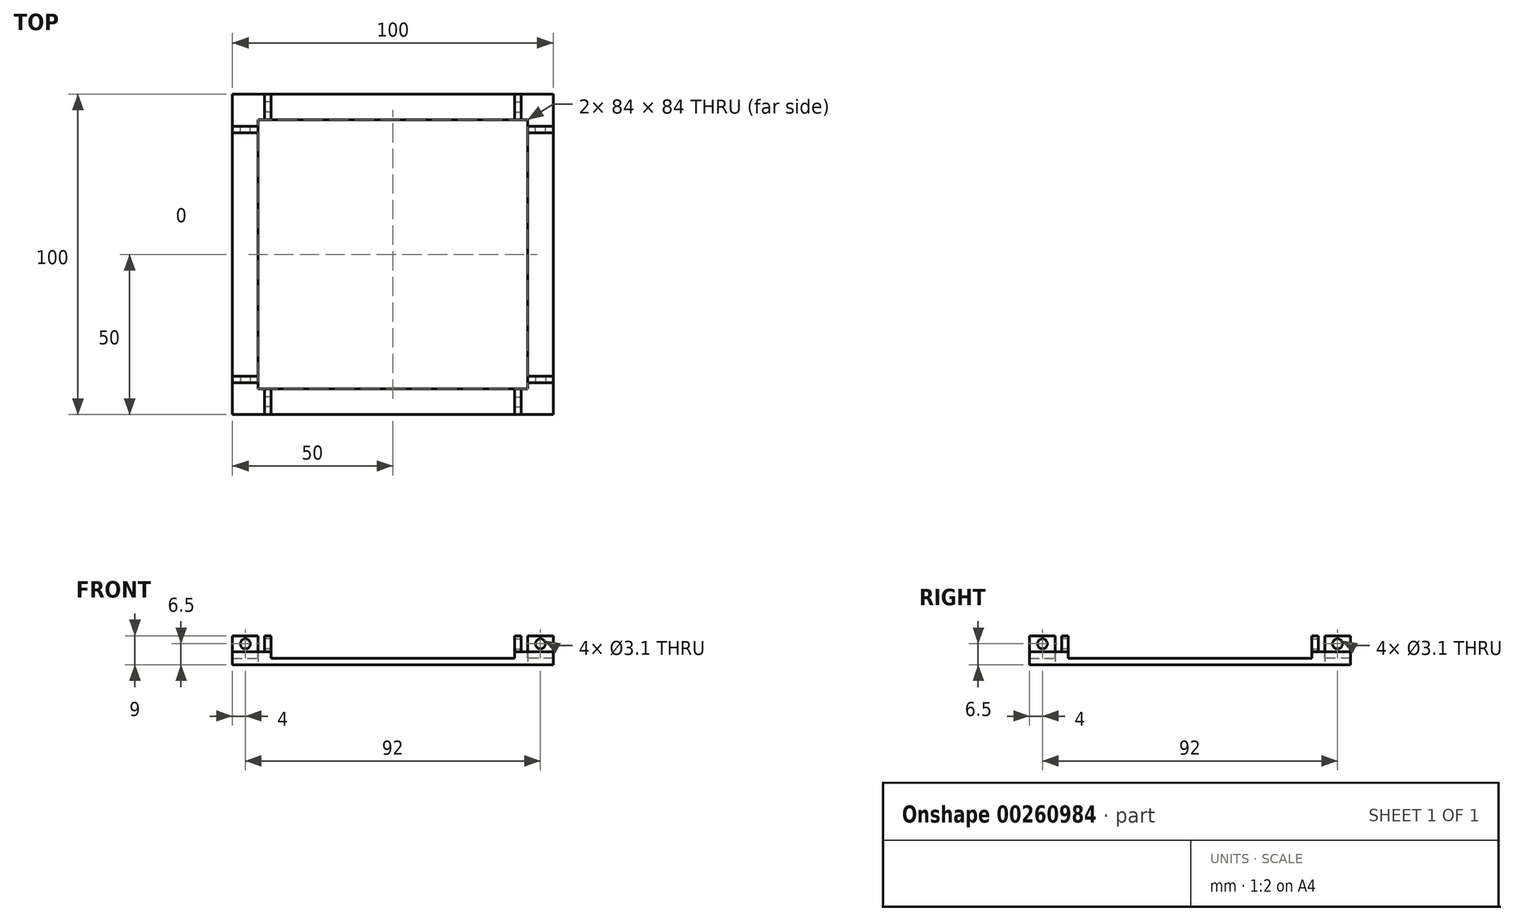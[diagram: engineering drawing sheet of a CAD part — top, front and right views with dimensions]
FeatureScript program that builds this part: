
annotation { "Feature Type Name" : "Feature", "Feature Type Description" : "" }
export const myFeature = defineFeature(function(context is Context, id is Id, definition is map)
    precondition{}
    {
        {
            var Q0;
            Q0=qCreatedBy(makeId("Top.planeOp"),FACE);
            var sketch = newSketch(context, id + "F0", { "sketchPlane" : qUnion([Q0])});
            skLineSegment(sketch, "E0", {"start": v(0, 0) * mm, "end": v(100, 0) * mm});
            skLineSegment(sketch, "E1", {"start": v(100, 0) * mm, "end": v(100, 100) * mm});
            skLineSegment(sketch, "E2", {"start": v(100, 100) * mm, "end": v(0, 100) * mm});
            skLineSegment(sketch, "E3", {"start": v(0, 100) * mm, "end": v(0, 0) * mm});
            skLineSegment(sketch, "E4", {"start": v(0, 0) * mm, "end": v(8, 0) * mm});
            skLineSegment(sketch, "E5", {"start": v(8, 8) * mm, "end": v(8, 92) * mm});
            skLineSegment(sketch, "E6", {"start": v(8, 92) * mm, "end": v(92, 92) * mm});
            skLineSegment(sketch, "E7", {"start": v(92, 92) * mm, "end": v(92, 8) * mm});
            skLineSegment(sketch, "E8", {"start": v(92, 8) * mm, "end": v(8, 8) * mm});
            skLineSegment(sketch, "E9", {"start": v(50, 0) * mm, "end": v(50, 8) * mm, "construction": true});
            skSolve(sketch);
        }
        {
            var Q0;
            Q0=makeQuery(id+"F0.imprint","IMPRINT",FACE,{"disambiguationData":[TD([[makeQuery(id+"F0.imprint","IMPRINT",EDGE,{"derivedFrom":sQuery(id+"F0.wireOp",EDGE,"E0")}),1.0]])]});
            extrude(context, id + "F1", {"entities" : qUnion([Q0]), "depth" : 8 * mm});
        }
        {
            var Q0;
            Q0=makeQuery(id+"F1.opExtrude","CAP_FACE",FACE,{"disambiguationData":[OSD([sQuery(id+"F0.wireOp",EDGE,"E0"),sQuery(id+"F0.wireOp",EDGE,"E1"),sQuery(id+"F0.wireOp",EDGE,"E2"),sQuery(id+"F0.wireOp",EDGE,"E3"),sQuery(id+"F0.wireOp",EDGE,"E4"),sQuery(id+"F0.wireOp",EDGE,"E5"),sQuery(id+"F0.wireOp",EDGE,"E6"),sQuery(id+"F0.wireOp",EDGE,"E7"),sQuery(id+"F0.wireOp",EDGE,"E8")])],"isStart":false});
            var sketch = newSketch(context, id + "F2", { "sketchPlane" : qUnion([Q0])});
            skLineSegment(sketch, "E10.0", {"start": v(92, 8) * mm, "end": v(8, 8) * mm, "construction": true});
            skLineSegment(sketch, "E11.0", {"start": v(0, 0) * mm, "end": v(100, 0) * mm, "construction": true});
            skLineSegment(sketch, "E12", {"start": v(8, 8) * mm, "end": v(8, 0) * mm});
            skLineSegment(sketch, "E13", {"start": v(8, 0) * mm, "end": v(12, 0) * mm});
            skLineSegment(sketch, "E14", {"start": v(12, 0) * mm, "end": v(12, 8) * mm});
            skLineSegment(sketch, "E15", {"start": v(12, 8) * mm, "end": v(8, 8) * mm});
            skSolve(sketch);
        }
        {
            var Q0;
            Q0=makeQuery(id+"F2.imprint","IMPRINT",FACE,{"disambiguationData":[TD([[makeQuery(id+"F2.imprint","IMPRINT",EDGE,{"derivedFrom":sQuery(id+"F2.wireOp",EDGE,"E12")}),1.0]])]});
            extrude(context, id + "F3", {"entities" : qUnion([Q0]), "operationType" : NewBodyOperationType.ADD, "depth" : 5 * mm});
        }
        {
            var Q0;
            Q0=makeQuery(id+"F3.opExtrude","SWEPT_FACE",FACE,{"disambiguationData":[OSD([sQuery(id+"F2.wireOp",EDGE,"E12")])]});
            var sketch = newSketch(context, id + "F4", { "sketchPlane" : qUnion([Q0])});
            skLineSegment(sketch, "E16.0", {"start": v(-8, 13) * mm, "end": v(0, 13) * mm, "construction": true});
            skLineSegment(sketch, "E17.0", {"start": v(-8, 13) * mm, "end": v(-8, 8) * mm, "construction": true});
            skLineSegment(sketch, "E18.0", {"start": v(-100, 8) * mm, "end": v(0, 8) * mm, "construction": true});
            skLineSegment(sketch, "E19.0", {"start": v(0, 13) * mm, "end": v(0, 8) * mm, "construction": true});
            skLineSegment(sketch, "E20", {"start": v(-4, 13) * mm, "end": v(-4, 8) * mm, "construction": true});
            skCircle(sketch, "E21", {"center": v(-4, 10.5) * mm, "radius": 1.55 * mm});
            skSolve(sketch);
        }
        {
            var Q0;
            Q0=makeQuery(id+"F4.imprint","IMPRINT",FACE,{"disambiguationData":[TD([[makeQuery(id+"F4.imprint","IMPRINT",EDGE,{"derivedFrom":sQuery(id+"F4.wireOp",EDGE,"53860cc5-d47c-4bca-ac85-03c5c8d22e110.MirrorCS")}),-1.0]])]});
            var Q1;
            Q1=makeQuery(id+"F4.imprint","IMPRINT",FACE,{"disambiguationData":[TD([[makeQuery(id+"F4.imprint","IMPRINT",EDGE,{"derivedFrom":sQuery(id+"F4.wireOp",EDGE,"E21")}),1.0]])]});
            var Q2;
            Q2=makeQuery(id+"F4.imprint","IMPRINT",FACE,{"disambiguationData":[TD([[makeQuery(id+"F4.imprint","IMPRINT",EDGE,{"derivedFrom":sQuery(id+"F4.wireOp",EDGE,"ADuCnaiS-x6I3-Dmo5-K39o-WolqJzbKUGD2")}),1.0]])]});
            extrude(context, id + "F5", {"entities" : qUnion([Q0, Q1, Q2]), "operationType" : NewBodyOperationType.REMOVE, "oppositeDirection" : true, "depth" : 5 * mm});
        }
        {
            var Q0;
            Q0=makeQuery(id+"F1.opExtrude","CAP_FACE",FACE,{"disambiguationData":[OSD([sQuery(id+"F0.wireOp",EDGE,"E0"),sQuery(id+"F0.wireOp",EDGE,"E1"),sQuery(id+"F0.wireOp",EDGE,"E2"),sQuery(id+"F0.wireOp",EDGE,"E3"),sQuery(id+"F0.wireOp",EDGE,"E4"),sQuery(id+"F0.wireOp",EDGE,"E5"),sQuery(id+"F0.wireOp",EDGE,"E6"),sQuery(id+"F0.wireOp",EDGE,"E7"),sQuery(id+"F0.wireOp",EDGE,"E8")])],"isStart":false});
            var sketch = newSketch(context, id + "F6", { "sketchPlane" : qUnion([Q0])});
            skLineSegment(sketch, "E22.0", {"start": v(12, 0) * mm, "end": v(100, 0) * mm});
            skLineSegment(sketch, "E23.0", {"start": v(12, 8) * mm, "end": v(8, 8) * mm, "construction": true});
            skLineSegment(sketch, "E24.0", {"start": v(0, 0) * mm, "end": v(8, 0) * mm, "construction": true});
            skLineSegment(sketch, "E25", {"start": v(12, 0) * mm, "end": v(50, 0) * mm});
            skLineSegment(sketch, "E26", {"start": v(50, 0) * mm, "end": v(50, 8) * mm});
            skLineSegment(sketch, "E27", {"start": v(50, 8) * mm, "end": v(52, 8) * mm});
            skLineSegment(sketch, "E28", {"start": v(52, 8) * mm, "end": v(52, 0) * mm});
            skSolve(sketch);
        }
        {
            var Q0;
            {var subQ0=sQuery(id+"F6.wireOp",EDGE,"E26");Q0=makeQuery(id+"F6.imprint","IMPRINT",FACE,{"disambiguationData":[TD([[makeQuery(id+"F6.imprint","IMPRINT",EDGE,{"derivedFrom":subQ0}),-1.0]])]});}
            extrude(context, id + "F7", {"entities" : qUnion([Q0]), "operationType" : NewBodyOperationType.ADD, "depth" : 25 * mm});
        }
        {
            var Q0;
            Q0=makeQuery(id+"F1.opExtrude","SWEPT_BODY",BODY,{"disambiguationData":[OSD([sQuery(id+"F0.wireOp",EDGE,"E0"),sQuery(id+"F0.wireOp",EDGE,"E1"),sQuery(id+"F0.wireOp",EDGE,"E2"),sQuery(id+"F0.wireOp",EDGE,"E3"),sQuery(id+"F0.wireOp",EDGE,"E4"),sQuery(id+"F0.wireOp",EDGE,"E5"),sQuery(id+"F0.wireOp",EDGE,"E6"),sQuery(id+"F0.wireOp",EDGE,"E7"),sQuery(id+"F0.wireOp",EDGE,"E8")])]});
            var Q1;
            Q1=makeQuery(id+"F7.opExtrude","SWEPT_FACE",FACE,{"disambiguationData":[OSD([sQuery(id+"F6.wireOp",EDGE,"E26")])]});
            mirror(context, id + "F8", {"operationType" : NewBodyOperationType.ADD, "entities" : qUnion([Q0]), "mirrorPlane" : qUnion([Q1])});
        }
        {
            var Q0;
            {var subQ0=makeQuery(id+"F7.boolean.opBoolean","MERGE",FACE,{"derivedFrom":[makeQuery(id+"F3.boolean.opBoolean","MERGE",FACE,{"derivedFrom":[makeQuery(id+"F1.opExtrude","SWEPT_FACE",FACE,{"disambiguationData":[OSD([sQuery(id+"F0.wireOp",EDGE,"E8")])]}),makeQuery(id+"F3.opExtrude","SWEPT_FACE",FACE,{"disambiguationData":[OSD([sQuery(id+"F2.wireOp",EDGE,"E15")])]})]}),makeQuery(id+"F7.opExtrude","SWEPT_FACE",FACE,{"disambiguationData":[OSD([sQuery(id+"F6.wireOp",EDGE,"E27")])]})]});Q0=makeQuery(id+"F8.boolean.opBoolean","MERGE",FACE,{"derivedFrom":[subQ0,makeQuery(id+"F8.opPattern","COPY",FACE,{"derivedFrom":subQ0,"instanceName":"1"})]});}
            var sketch = newSketch(context, id + "F9", { "sketchPlane" : qUnion([Q0])});
            skLineSegment(sketch, "E29", {"start": v(-48, 8) * mm, "end": v(-50, 8) * mm});
            skLineSegment(sketch, "E30", {"start": v(-50, 8) * mm, "end": v(-50, 33) * mm});
            skLineSegment(sketch, "E31", {"start": v(-50, 33) * mm, "end": v(-48, 33) * mm});
            skLineSegment(sketch, "E32", {"start": v(-48, 33) * mm, "end": v(-48, 8) * mm});
            skSolve(sketch);
        }
        {
            var Q0;
            Q0=makeQuery(id+"F9.imprint","IMPRINT",FACE,{"disambiguationData":[TD([[makeQuery(id+"F9.imprint","IMPRINT",EDGE,{"derivedFrom":sQuery(id+"F9.wireOp",EDGE,"E29")}),-1.0]])]});
            extrude(context, id + "F10", {"entities" : qUnion([Q0]), "operationType" : NewBodyOperationType.ADD, "depth" : 42 * mm});
        }
        {
            var Q0;
            Q0=makeQuery(id+"F1.opExtrude","SWEPT_BODY",BODY,{"disambiguationData":[OSD([sQuery(id+"F0.wireOp",EDGE,"E0"),sQuery(id+"F0.wireOp",EDGE,"E1"),sQuery(id+"F0.wireOp",EDGE,"E2"),sQuery(id+"F0.wireOp",EDGE,"E3"),sQuery(id+"F0.wireOp",EDGE,"E4"),sQuery(id+"F0.wireOp",EDGE,"E5"),sQuery(id+"F0.wireOp",EDGE,"E6"),sQuery(id+"F0.wireOp",EDGE,"E7"),sQuery(id+"F0.wireOp",EDGE,"E8")])]});
            var Q1;
            Q1=makeQuery(id+"F10.opExtrude","CAP_EDGE",EDGE,{"disambiguationData":[OSD([sQuery(id+"F9.wireOp",EDGE,"E30")])],"isStart":false});
            circularPattern(context, id + "F11", {"entities" : qUnion([Q0]), "axis" : qUnion([Q1]), "angle" : 360 * degree, "instanceCount" : 4, "equalSpace" : true});
        }
        {
            var Q0;
            {var subQ0=makeQuery(id+"F7.opExtrude","CAP_FACE",FACE,{"disambiguationData":[OSD([sQuery(id+"F6.wireOp",EDGE,"E22.0"),sQuery(id+"F6.wireOp",EDGE,"E26"),sQuery(id+"F6.wireOp",EDGE,"E27"),sQuery(id+"F6.wireOp",EDGE,"E28")])],"isStart":false});Q0=makeQuery(id+"F11.opPattern","COPY",FACE,{"derivedFrom":makeQuery(id+"F10.boolean.opBoolean","MERGE",FACE,{"derivedFrom":[makeQuery(id+"F8.boolean.opBoolean","MERGE",FACE,{"derivedFrom":[subQ0,makeQuery(id+"F8.opPattern","COPY",FACE,{"derivedFrom":subQ0,"instanceName":"1"})]}),makeQuery(id+"F10.opExtrude","SWEPT_FACE",FACE,{"disambiguationData":[OSD([sQuery(id+"F9.wireOp",EDGE,"E31")])]})]}),"instanceName":"1"});}
            var Q1;
            {var subQ0=makeQuery(id+"F7.opExtrude","CAP_FACE",FACE,{"disambiguationData":[OSD([sQuery(id+"F6.wireOp",EDGE,"E22.0"),sQuery(id+"F6.wireOp",EDGE,"E26"),sQuery(id+"F6.wireOp",EDGE,"E27"),sQuery(id+"F6.wireOp",EDGE,"E28")])],"isStart":false});Q1=makeQuery(id+"F11.opPattern","COPY",FACE,{"derivedFrom":makeQuery(id+"F10.boolean.opBoolean","MERGE",FACE,{"derivedFrom":[makeQuery(id+"F8.boolean.opBoolean","MERGE",FACE,{"derivedFrom":[subQ0,makeQuery(id+"F8.opPattern","COPY",FACE,{"derivedFrom":subQ0,"instanceName":"1"})]}),makeQuery(id+"F10.opExtrude","SWEPT_FACE",FACE,{"disambiguationData":[OSD([sQuery(id+"F9.wireOp",EDGE,"E31")])]})]}),"instanceName":"2"});}
            var Q2;
            {var subQ0=makeQuery(id+"F7.opExtrude","CAP_FACE",FACE,{"disambiguationData":[OSD([sQuery(id+"F6.wireOp",EDGE,"E22.0"),sQuery(id+"F6.wireOp",EDGE,"E26"),sQuery(id+"F6.wireOp",EDGE,"E27"),sQuery(id+"F6.wireOp",EDGE,"E28")])],"isStart":false});Q2=makeQuery(id+"F11.opPattern","COPY",FACE,{"derivedFrom":makeQuery(id+"F10.boolean.opBoolean","MERGE",FACE,{"derivedFrom":[makeQuery(id+"F8.boolean.opBoolean","MERGE",FACE,{"derivedFrom":[subQ0,makeQuery(id+"F8.opPattern","COPY",FACE,{"derivedFrom":subQ0,"instanceName":"1"})]}),makeQuery(id+"F10.opExtrude","SWEPT_FACE",FACE,{"disambiguationData":[OSD([sQuery(id+"F9.wireOp",EDGE,"E31")])]})]}),"instanceName":"3"});}
            var Q3;
            {var subQ0=makeQuery(id+"F7.opExtrude","CAP_FACE",FACE,{"disambiguationData":[OSD([sQuery(id+"F6.wireOp",EDGE,"E22.0"),sQuery(id+"F6.wireOp",EDGE,"E26"),sQuery(id+"F6.wireOp",EDGE,"E27"),sQuery(id+"F6.wireOp",EDGE,"E28")])],"isStart":false});Q3=makeQuery(id+"F10.boolean.opBoolean","MERGE",FACE,{"derivedFrom":[makeQuery(id+"F8.boolean.opBoolean","MERGE",FACE,{"derivedFrom":[subQ0,makeQuery(id+"F8.opPattern","COPY",FACE,{"derivedFrom":subQ0,"instanceName":"1"})]}),makeQuery(id+"F10.opExtrude","SWEPT_FACE",FACE,{"disambiguationData":[OSD([sQuery(id+"F9.wireOp",EDGE,"E31")])]})]});}
            extrude(context, id + "F12", {"entities" : qUnion([Q0, Q1, Q2, Q3]), "operationType" : NewBodyOperationType.REMOVE, "oppositeDirection" : true, "depth" : 25 * mm});
        }
        {
            var Q0;
            Q0=makeQuery(id+"F11.opPattern","COPY",FACE,{"derivedFrom":makeQuery(id+"F3.opExtrude","SWEPT_FACE",FACE,{"disambiguationData":[OSD([sQuery(id+"F2.wireOp",EDGE,"E12")])]}),"instanceName":"2"});
            var Q1;
            Q1=makeQuery(id+"F8.opPattern","COPY",FACE,{"derivedFrom":makeQuery(id+"F3.opExtrude","SWEPT_FACE",FACE,{"disambiguationData":[OSD([sQuery(id+"F2.wireOp",EDGE,"E12")])]}),"instanceName":"1"});
            extrude(context, id + "F13", {"entities" : qUnion([Q0, Q1]), "operationType" : NewBodyOperationType.REMOVE, "oppositeDirection" : true, "depth" : 2 * mm});
        }
        {
            var Q0;
            Q0=makeQuery(id+"F11.opPattern","COPY",FACE,{"derivedFrom":makeQuery(id+"F3.opExtrude","SWEPT_FACE",FACE,{"disambiguationData":[OSD([sQuery(id+"F2.wireOp",EDGE,"E12")])]}),"instanceName":"1"});
            var Q1;
            Q1=makeQuery(id+"F11.opPattern","COPY",FACE,{"derivedFrom":makeQuery(id+"F8.opPattern","COPY",FACE,{"derivedFrom":makeQuery(id+"F3.opExtrude","SWEPT_FACE",FACE,{"disambiguationData":[OSD([sQuery(id+"F2.wireOp",EDGE,"E12")])]}),"instanceName":"1"}),"instanceName":"3"});
            extrude(context, id + "F14", {"entities" : qUnion([Q0, Q1]), "operationType" : NewBodyOperationType.REMOVE, "oppositeDirection" : true, "depth" : 2 * mm});
        }
        {
            var Q0;
            Q0=makeQuery(id+"F3.opExtrude","SWEPT_FACE",FACE,{"disambiguationData":[OSD([sQuery(id+"F2.wireOp",EDGE,"E12")])]});
            var Q1;
            Q1=makeQuery(id+"F11.opPattern","COPY",FACE,{"derivedFrom":makeQuery(id+"F8.opPattern","COPY",FACE,{"derivedFrom":makeQuery(id+"F3.opExtrude","SWEPT_FACE",FACE,{"disambiguationData":[OSD([sQuery(id+"F2.wireOp",EDGE,"E12")])]}),"instanceName":"1"}),"instanceName":"2"});
            extrude(context, id + "F15", {"entities" : qUnion([Q0, Q1]), "operationType" : NewBodyOperationType.REMOVE, "oppositeDirection" : true, "depth" : 2 * mm});
        }
        {
            var Q0;
            Q0=makeQuery(id+"F11.opPattern","COPY",FACE,{"derivedFrom":makeQuery(id+"F8.opPattern","COPY",FACE,{"derivedFrom":makeQuery(id+"F3.opExtrude","SWEPT_FACE",FACE,{"disambiguationData":[OSD([sQuery(id+"F2.wireOp",EDGE,"E12")])]}),"instanceName":"1"}),"instanceName":"1"});
            var Q1;
            Q1=makeQuery(id+"F11.opPattern","COPY",FACE,{"derivedFrom":makeQuery(id+"F3.opExtrude","SWEPT_FACE",FACE,{"disambiguationData":[OSD([sQuery(id+"F2.wireOp",EDGE,"E12")])]}),"instanceName":"3"});
            extrude(context, id + "F16", {"entities" : qUnion([Q0, Q1]), "operationType" : NewBodyOperationType.REMOVE, "oppositeDirection" : true, "depth" : 2 * mm});
        }
        {
            var Q0;
            Q0=makeQuery(id+"F11.opPattern","COPY",FACE,{"derivedFrom":makeQuery(id+"F1.opExtrude","CAP_FACE",FACE,{"disambiguationData":[OSD([sQuery(id+"F0.wireOp",EDGE,"E0"),sQuery(id+"F0.wireOp",EDGE,"E1"),sQuery(id+"F0.wireOp",EDGE,"E2"),sQuery(id+"F0.wireOp",EDGE,"E3"),sQuery(id+"F0.wireOp",EDGE,"E4"),sQuery(id+"F0.wireOp",EDGE,"E5"),sQuery(id+"F0.wireOp",EDGE,"E6"),sQuery(id+"F0.wireOp",EDGE,"E7"),sQuery(id+"F0.wireOp",EDGE,"E8")])],"isStart":true}),"instanceName":"2"});
            extrude(context, id + "F17", {"entities" : qUnion([Q0]), "operationType" : NewBodyOperationType.REMOVE, "oppositeDirection" : true, "depth" : 4 * mm});
        }
        {
            var Q0;
            {var subQ0=sQuery(id+"F9.wireOp",EDGE,"E31");var subQ1=sQuery(id+"F6.wireOp",EDGE,"E28");var subQ2=sQuery(id+"F6.wireOp",EDGE,"E27");var subQ3=sQuery(id+"F6.wireOp",EDGE,"E26");var subQ4=sQuery(id+"F6.wireOp",EDGE,"E22.0");var subQ5=makeQuery(id+"F7.opExtrude","CAP_FACE",FACE,{"disambiguationData":[OSD([subQ4,subQ3,subQ2,subQ1])],"isStart":false});var subQ6=makeQuery(id+"F10.boolean.opBoolean","MERGE",FACE,{"derivedFrom":[makeQuery(id+"F8.boolean.opBoolean","MERGE",FACE,{"derivedFrom":[subQ5,makeQuery(id+"F8.opPattern","COPY",FACE,{"derivedFrom":subQ5,"instanceName":"1"})]}),makeQuery(id+"F10.opExtrude","SWEPT_FACE",FACE,{"disambiguationData":[OSD([subQ0])]})]});var subQ10=sQuery(id+"F0.wireOp",EDGE,"E8");var subQ12=sQuery(id+"F0.wireOp",EDGE,"E4");var subQ13=sQuery(id+"F0.wireOp",EDGE,"E0");var subQ16=makeQuery(id+"F7.opExtrude","SWEPT_FACE",FACE,{"disambiguationData":[OSD([subQ1])]});var subQ17=makeQuery(id+"F3.opExtrude","SWEPT_FACE",FACE,{"disambiguationData":[OSD([sQuery(id+"F2.wireOp",EDGE,"E14")])]});var subQ18=sQuery(id+"F0.wireOp",EDGE,"E2");var subQ19=sQuery(id+"F0.wireOp",EDGE,"E7");var subQ20=sQuery(id+"F0.wireOp",EDGE,"E6");var subQ21=sQuery(id+"F0.wireOp",EDGE,"E5");var subQ22=sQuery(id+"F0.wireOp",EDGE,"E1");var subQ23=sQuery(id+"F0.wireOp",EDGE,"E3");var subQ24=makeQuery(id+"F1.opExtrude","CAP_FACE",FACE,{"disambiguationData":[OSD([subQ13,subQ22,subQ18,subQ23,subQ12,subQ21,subQ20,subQ19,subQ10])],"isStart":false});Q0=makeQuery(id+"F12.boolean.opBoolean","MERGE",FACE,{"derivedFrom":[makeQuery(id+"F11.opPattern","COPY",FACE,{"derivedFrom":makeQuery(id+"F7.boolean.opBoolean","SPLIT",FACE,{"disambiguationData":[TD([subQ17])],"derivedFrom":subQ24}),"instanceName":"1"}),makeQuery(id+"F11.opPattern","COPY",FACE,{"derivedFrom":makeQuery(id+"F8.boolean.opBoolean","SPLIT",FACE,{"disambiguationData":[TD([subQ16])],"derivedFrom":makeQuery(id+"F7.boolean.opBoolean","SPLIT",FACE,{"disambiguationData":[TD([makeQuery(id+"F1.opExtrude","SWEPT_FACE",FACE,{"disambiguationData":[OSD([subQ22])]})])],"derivedFrom":subQ24})}),"instanceName":"1"}),makeQuery(id+"F12.opExtrude","CAP_FACE",FACE,{"disambiguationData":[OSD([subQ4,subQ3,subQ2,subQ1,subQ0]),TDD([subQ6])],"isStart":false}),makeQuery(id+"F12.opExtrude","CAP_FACE",FACE,{"disambiguationData":[OSD([subQ4,subQ3,subQ2,subQ1,subQ0]),TDD([makeQuery(id+"F11.opPattern","COPY",FACE,{"derivedFrom":subQ6,"instanceName":"1"})])],"isStart":false}),makeQuery(id+"F12.opExtrude","CAP_FACE",FACE,{"disambiguationData":[OSD([subQ4,subQ3,subQ2,subQ1,subQ0]),TDD([makeQuery(id+"F11.opPattern","COPY",FACE,{"derivedFrom":subQ6,"instanceName":"2"})])],"isStart":false}),makeQuery(id+"F12.opExtrude","CAP_FACE",FACE,{"disambiguationData":[OSD([subQ4,subQ3,subQ2,subQ1,subQ0]),TDD([makeQuery(id+"F11.opPattern","COPY",FACE,{"derivedFrom":subQ6,"instanceName":"3"})])],"isStart":false})]});}
            var Q1;
            {var subQ0=sQuery(id+"F9.wireOp",EDGE,"E31");var subQ1=sQuery(id+"F6.wireOp",EDGE,"E28");var subQ2=sQuery(id+"F6.wireOp",EDGE,"E27");var subQ3=sQuery(id+"F6.wireOp",EDGE,"E26");var subQ4=sQuery(id+"F6.wireOp",EDGE,"E22.0");var subQ5=makeQuery(id+"F7.opExtrude","CAP_FACE",FACE,{"disambiguationData":[OSD([subQ4,subQ3,subQ2,subQ1])],"isStart":false});var subQ6=makeQuery(id+"F10.boolean.opBoolean","MERGE",FACE,{"derivedFrom":[makeQuery(id+"F8.boolean.opBoolean","MERGE",FACE,{"derivedFrom":[subQ5,makeQuery(id+"F8.opPattern","COPY",FACE,{"derivedFrom":subQ5,"instanceName":"1"})]}),makeQuery(id+"F10.opExtrude","SWEPT_FACE",FACE,{"disambiguationData":[OSD([subQ0])]})]});var subQ10=sQuery(id+"F0.wireOp",EDGE,"E8");var subQ12=sQuery(id+"F0.wireOp",EDGE,"E4");var subQ13=sQuery(id+"F0.wireOp",EDGE,"E0");var subQ16=makeQuery(id+"F7.opExtrude","SWEPT_FACE",FACE,{"disambiguationData":[OSD([subQ1])]});var subQ17=makeQuery(id+"F3.opExtrude","SWEPT_FACE",FACE,{"disambiguationData":[OSD([sQuery(id+"F2.wireOp",EDGE,"E14")])]});var subQ18=sQuery(id+"F0.wireOp",EDGE,"E2");var subQ19=sQuery(id+"F0.wireOp",EDGE,"E7");var subQ20=sQuery(id+"F0.wireOp",EDGE,"E6");var subQ21=sQuery(id+"F0.wireOp",EDGE,"E5");var subQ22=sQuery(id+"F0.wireOp",EDGE,"E1");var subQ23=sQuery(id+"F0.wireOp",EDGE,"E3");var subQ24=makeQuery(id+"F1.opExtrude","CAP_FACE",FACE,{"disambiguationData":[OSD([subQ13,subQ22,subQ18,subQ23,subQ12,subQ21,subQ20,subQ19,subQ10])],"isStart":false});Q1=makeQuery(id+"F12.boolean.opBoolean","MERGE",FACE,{"derivedFrom":[makeQuery(id+"F7.boolean.opBoolean","SPLIT",FACE,{"disambiguationData":[TD([subQ17])],"derivedFrom":subQ24}),makeQuery(id+"F8.boolean.opBoolean","SPLIT",FACE,{"disambiguationData":[TD([subQ16])],"derivedFrom":makeQuery(id+"F7.boolean.opBoolean","SPLIT",FACE,{"disambiguationData":[TD([makeQuery(id+"F1.opExtrude","SWEPT_FACE",FACE,{"disambiguationData":[OSD([subQ22])]})])],"derivedFrom":subQ24})}),makeQuery(id+"F12.opExtrude","CAP_FACE",FACE,{"disambiguationData":[OSD([subQ4,subQ3,subQ2,subQ1,subQ0]),TDD([subQ6])],"isStart":false}),makeQuery(id+"F12.opExtrude","CAP_FACE",FACE,{"disambiguationData":[OSD([subQ4,subQ3,subQ2,subQ1,subQ0]),TDD([makeQuery(id+"F11.opPattern","COPY",FACE,{"derivedFrom":subQ6,"instanceName":"1"})])],"isStart":false}),makeQuery(id+"F12.opExtrude","CAP_FACE",FACE,{"disambiguationData":[OSD([subQ4,subQ3,subQ2,subQ1,subQ0]),TDD([makeQuery(id+"F11.opPattern","COPY",FACE,{"derivedFrom":subQ6,"instanceName":"2"})])],"isStart":false}),makeQuery(id+"F12.opExtrude","CAP_FACE",FACE,{"disambiguationData":[OSD([subQ4,subQ3,subQ2,subQ1,subQ0]),TDD([makeQuery(id+"F11.opPattern","COPY",FACE,{"derivedFrom":subQ6,"instanceName":"3"})])],"isStart":false})]});}
            var Q2;
            {var subQ0=sQuery(id+"F9.wireOp",EDGE,"E31");var subQ1=sQuery(id+"F6.wireOp",EDGE,"E28");var subQ2=sQuery(id+"F6.wireOp",EDGE,"E27");var subQ3=sQuery(id+"F6.wireOp",EDGE,"E26");var subQ4=sQuery(id+"F6.wireOp",EDGE,"E22.0");var subQ5=makeQuery(id+"F7.opExtrude","CAP_FACE",FACE,{"disambiguationData":[OSD([subQ4,subQ3,subQ2,subQ1])],"isStart":false});var subQ6=makeQuery(id+"F10.boolean.opBoolean","MERGE",FACE,{"derivedFrom":[makeQuery(id+"F8.boolean.opBoolean","MERGE",FACE,{"derivedFrom":[subQ5,makeQuery(id+"F8.opPattern","COPY",FACE,{"derivedFrom":subQ5,"instanceName":"1"})]}),makeQuery(id+"F10.opExtrude","SWEPT_FACE",FACE,{"disambiguationData":[OSD([subQ0])]})]});var subQ10=sQuery(id+"F0.wireOp",EDGE,"E8");var subQ12=sQuery(id+"F0.wireOp",EDGE,"E4");var subQ13=sQuery(id+"F0.wireOp",EDGE,"E0");var subQ16=makeQuery(id+"F7.opExtrude","SWEPT_FACE",FACE,{"disambiguationData":[OSD([subQ1])]});var subQ17=makeQuery(id+"F3.opExtrude","SWEPT_FACE",FACE,{"disambiguationData":[OSD([sQuery(id+"F2.wireOp",EDGE,"E14")])]});var subQ18=sQuery(id+"F0.wireOp",EDGE,"E2");var subQ19=sQuery(id+"F0.wireOp",EDGE,"E7");var subQ20=sQuery(id+"F0.wireOp",EDGE,"E6");var subQ21=sQuery(id+"F0.wireOp",EDGE,"E5");var subQ22=sQuery(id+"F0.wireOp",EDGE,"E1");var subQ23=sQuery(id+"F0.wireOp",EDGE,"E3");var subQ24=makeQuery(id+"F1.opExtrude","CAP_FACE",FACE,{"disambiguationData":[OSD([subQ13,subQ22,subQ18,subQ23,subQ12,subQ21,subQ20,subQ19,subQ10])],"isStart":false});Q2=makeQuery(id+"F12.boolean.opBoolean","MERGE",FACE,{"derivedFrom":[makeQuery(id+"F11.opPattern","COPY",FACE,{"derivedFrom":makeQuery(id+"F7.boolean.opBoolean","SPLIT",FACE,{"disambiguationData":[TD([subQ17])],"derivedFrom":subQ24}),"instanceName":"2"}),makeQuery(id+"F11.opPattern","COPY",FACE,{"derivedFrom":makeQuery(id+"F8.boolean.opBoolean","SPLIT",FACE,{"disambiguationData":[TD([subQ16])],"derivedFrom":makeQuery(id+"F7.boolean.opBoolean","SPLIT",FACE,{"disambiguationData":[TD([makeQuery(id+"F1.opExtrude","SWEPT_FACE",FACE,{"disambiguationData":[OSD([subQ22])]})])],"derivedFrom":subQ24})}),"instanceName":"2"}),makeQuery(id+"F12.opExtrude","CAP_FACE",FACE,{"disambiguationData":[OSD([subQ4,subQ3,subQ2,subQ1,subQ0]),TDD([subQ6])],"isStart":false}),makeQuery(id+"F12.opExtrude","CAP_FACE",FACE,{"disambiguationData":[OSD([subQ4,subQ3,subQ2,subQ1,subQ0]),TDD([makeQuery(id+"F11.opPattern","COPY",FACE,{"derivedFrom":subQ6,"instanceName":"1"})])],"isStart":false}),makeQuery(id+"F12.opExtrude","CAP_FACE",FACE,{"disambiguationData":[OSD([subQ4,subQ3,subQ2,subQ1,subQ0]),TDD([makeQuery(id+"F11.opPattern","COPY",FACE,{"derivedFrom":subQ6,"instanceName":"2"})])],"isStart":false}),makeQuery(id+"F12.opExtrude","CAP_FACE",FACE,{"disambiguationData":[OSD([subQ4,subQ3,subQ2,subQ1,subQ0]),TDD([makeQuery(id+"F11.opPattern","COPY",FACE,{"derivedFrom":subQ6,"instanceName":"3"})])],"isStart":false})]});}
            var Q3;
            {var subQ0=sQuery(id+"F9.wireOp",EDGE,"E31");var subQ1=sQuery(id+"F6.wireOp",EDGE,"E28");var subQ2=sQuery(id+"F6.wireOp",EDGE,"E27");var subQ3=sQuery(id+"F6.wireOp",EDGE,"E26");var subQ4=sQuery(id+"F6.wireOp",EDGE,"E22.0");var subQ5=makeQuery(id+"F7.opExtrude","CAP_FACE",FACE,{"disambiguationData":[OSD([subQ4,subQ3,subQ2,subQ1])],"isStart":false});var subQ6=makeQuery(id+"F10.boolean.opBoolean","MERGE",FACE,{"derivedFrom":[makeQuery(id+"F8.boolean.opBoolean","MERGE",FACE,{"derivedFrom":[subQ5,makeQuery(id+"F8.opPattern","COPY",FACE,{"derivedFrom":subQ5,"instanceName":"1"})]}),makeQuery(id+"F10.opExtrude","SWEPT_FACE",FACE,{"disambiguationData":[OSD([subQ0])]})]});var subQ10=sQuery(id+"F0.wireOp",EDGE,"E8");var subQ12=sQuery(id+"F0.wireOp",EDGE,"E4");var subQ13=sQuery(id+"F0.wireOp",EDGE,"E0");var subQ16=makeQuery(id+"F7.opExtrude","SWEPT_FACE",FACE,{"disambiguationData":[OSD([subQ1])]});var subQ17=makeQuery(id+"F3.opExtrude","SWEPT_FACE",FACE,{"disambiguationData":[OSD([sQuery(id+"F2.wireOp",EDGE,"E14")])]});var subQ18=sQuery(id+"F0.wireOp",EDGE,"E2");var subQ19=sQuery(id+"F0.wireOp",EDGE,"E7");var subQ20=sQuery(id+"F0.wireOp",EDGE,"E6");var subQ21=sQuery(id+"F0.wireOp",EDGE,"E5");var subQ22=sQuery(id+"F0.wireOp",EDGE,"E1");var subQ23=sQuery(id+"F0.wireOp",EDGE,"E3");var subQ24=makeQuery(id+"F1.opExtrude","CAP_FACE",FACE,{"disambiguationData":[OSD([subQ13,subQ22,subQ18,subQ23,subQ12,subQ21,subQ20,subQ19,subQ10])],"isStart":false});Q3=makeQuery(id+"F12.boolean.opBoolean","MERGE",FACE,{"derivedFrom":[makeQuery(id+"F11.opPattern","COPY",FACE,{"derivedFrom":makeQuery(id+"F7.boolean.opBoolean","SPLIT",FACE,{"disambiguationData":[TD([subQ17])],"derivedFrom":subQ24}),"instanceName":"3"}),makeQuery(id+"F11.opPattern","COPY",FACE,{"derivedFrom":makeQuery(id+"F8.boolean.opBoolean","SPLIT",FACE,{"disambiguationData":[TD([subQ16])],"derivedFrom":makeQuery(id+"F7.boolean.opBoolean","SPLIT",FACE,{"disambiguationData":[TD([makeQuery(id+"F1.opExtrude","SWEPT_FACE",FACE,{"disambiguationData":[OSD([subQ22])]})])],"derivedFrom":subQ24})}),"instanceName":"3"}),makeQuery(id+"F12.opExtrude","CAP_FACE",FACE,{"disambiguationData":[OSD([subQ4,subQ3,subQ2,subQ1,subQ0]),TDD([subQ6])],"isStart":false}),makeQuery(id+"F12.opExtrude","CAP_FACE",FACE,{"disambiguationData":[OSD([subQ4,subQ3,subQ2,subQ1,subQ0]),TDD([makeQuery(id+"F11.opPattern","COPY",FACE,{"derivedFrom":subQ6,"instanceName":"1"})])],"isStart":false}),makeQuery(id+"F12.opExtrude","CAP_FACE",FACE,{"disambiguationData":[OSD([subQ4,subQ3,subQ2,subQ1,subQ0]),TDD([makeQuery(id+"F11.opPattern","COPY",FACE,{"derivedFrom":subQ6,"instanceName":"2"})])],"isStart":false}),makeQuery(id+"F12.opExtrude","CAP_FACE",FACE,{"disambiguationData":[OSD([subQ4,subQ3,subQ2,subQ1,subQ0]),TDD([makeQuery(id+"F11.opPattern","COPY",FACE,{"derivedFrom":subQ6,"instanceName":"3"})])],"isStart":false})]});}
            extrude(context, id + "F18", {"entities" : qUnion([Q0, Q1, Q2, Q3]), "operationType" : NewBodyOperationType.REMOVE, "oppositeDirection" : true, "depth" : 2 * mm, "offsetDistance" : 25 * mm});
        }
    });
